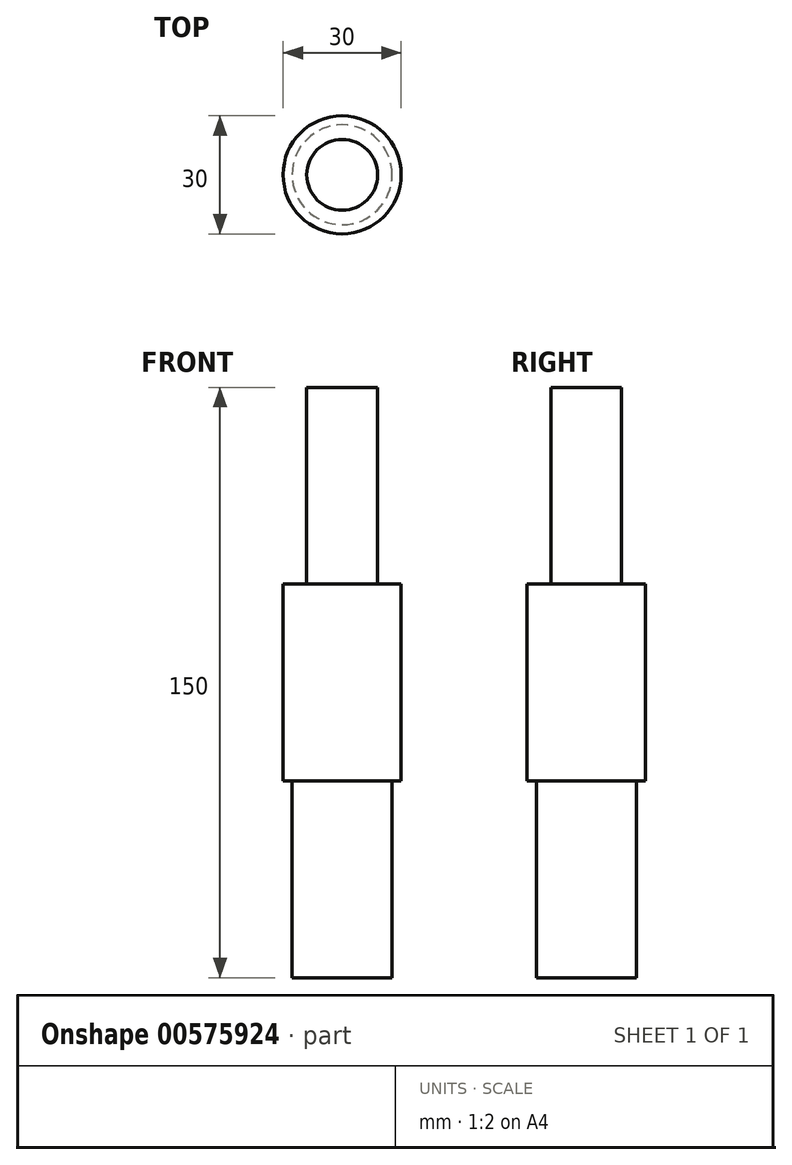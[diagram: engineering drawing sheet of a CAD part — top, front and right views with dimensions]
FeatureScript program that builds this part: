
annotation { "Feature Type Name" : "Feature", "Feature Type Description" : "" }
export const myFeature = defineFeature(function(context is Context, id is Id, definition is map)
    precondition{}
    {
        {
            var Q0;
            Q0=qCreatedBy(makeId("Front.planeOp"),FACE);
            var sketch = newSketch(context, id + "F0", { "sketchPlane" : qUnion([Q0])});
            skLineSegment(sketch, "E0", {"start": v(0, 0) * mm, "end": v(0, 150) * mm});
            skLineSegment(sketch, "E1", {"start": v(0, 150) * mm, "end": v(9, 150) * mm});
            skLineSegment(sketch, "E2", {"start": v(9, 150) * mm, "end": v(9, 100) * mm});
            skLineSegment(sketch, "E3", {"start": v(9, 100) * mm, "end": v(15, 100) * mm});
            skLineSegment(sketch, "E4", {"start": v(15, 100) * mm, "end": v(15, 50) * mm});
            skLineSegment(sketch, "E5", {"start": v(15, 50) * mm, "end": v(12.7, 50) * mm});
            skLineSegment(sketch, "E6", {"start": v(12.7, 50) * mm, "end": v(12.7, 0) * mm});
            skLineSegment(sketch, "E7", {"start": v(12.7, 0) * mm, "end": v(0, 0) * mm});
            skSolve(sketch);
        }
        {
            var Q0;
            Q0=makeQuery(id+"F0.imprint","IMPRINT",FACE,{"disambiguationData":[TD([[makeQuery(id+"F0.imprint","IMPRINT",EDGE,{"derivedFrom":sQuery(id+"F0.wireOp",EDGE,"E0")}),-1.0]])]});
            var Q1;
            Q1=sQuery(id+"F0.wireOp",EDGE,"E0");
            revolve(context, id + "F1", {"entities" : qUnion([Q0]), "axis" : qUnion([Q1]), "revolveType" : RevolveType.FULL});
        }
    });
